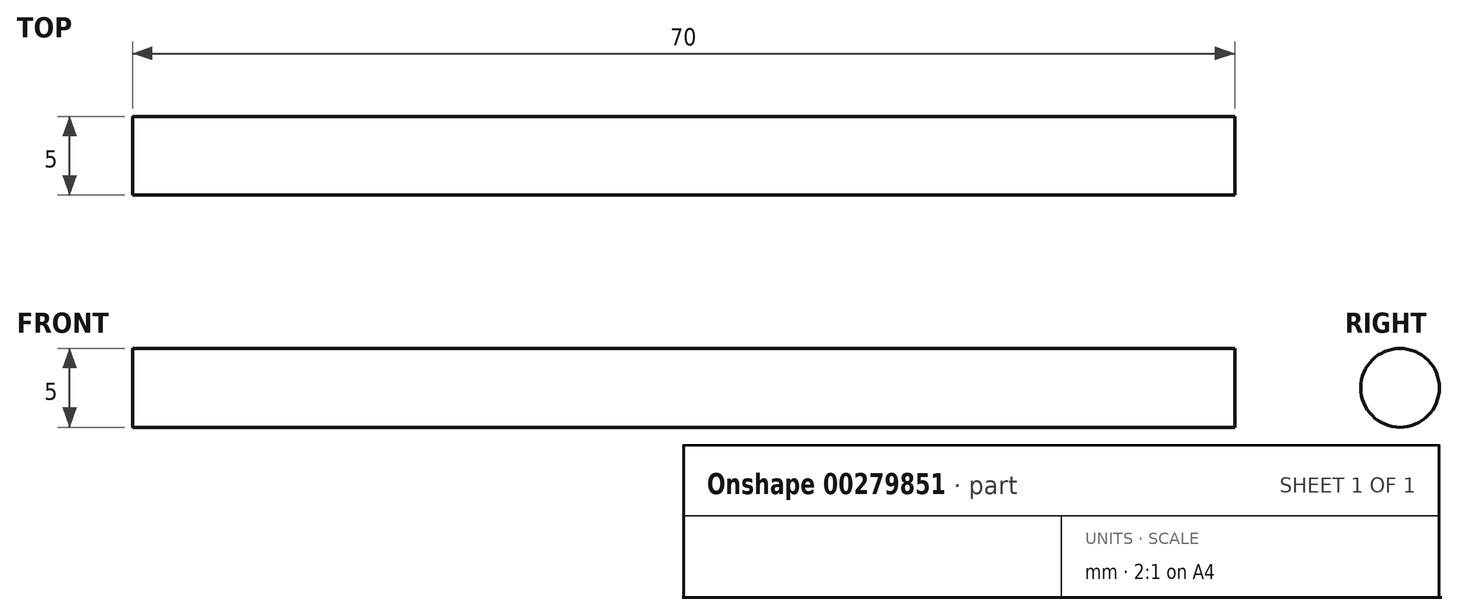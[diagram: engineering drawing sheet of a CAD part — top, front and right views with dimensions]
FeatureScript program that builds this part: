
annotation { "Feature Type Name" : "Feature", "Feature Type Description" : "" }
export const myFeature = defineFeature(function(context is Context, id is Id, definition is map)
    precondition{}
    {
        {
            var Q0;
            Q0=qCreatedBy(makeId("Right.planeOp"),FACE);
            var sketch = newSketch(context, id + "F0", { "sketchPlane" : qUnion([Q0])});
            skCircle(sketch, "E0", {"center": v(0, 0) * mm, "radius": 2.5 * mm});
            skSolve(sketch);
        }
        {
            var Q0;
            Q0=makeQuery(id+"F0.imprint","IMPRINT",FACE,{"disambiguationData":[TD([[makeQuery(id+"F0.imprint","IMPRINT",EDGE,{"derivedFrom":sQuery(id+"F0.wireOp",EDGE,"E0")}),1.0]])]});
            extrude(context, id + "F1", {"entities" : qUnion([Q0]), "endBound" : BoundingType.SYMMETRIC, "depth" : 70 * mm});
        }
    });
